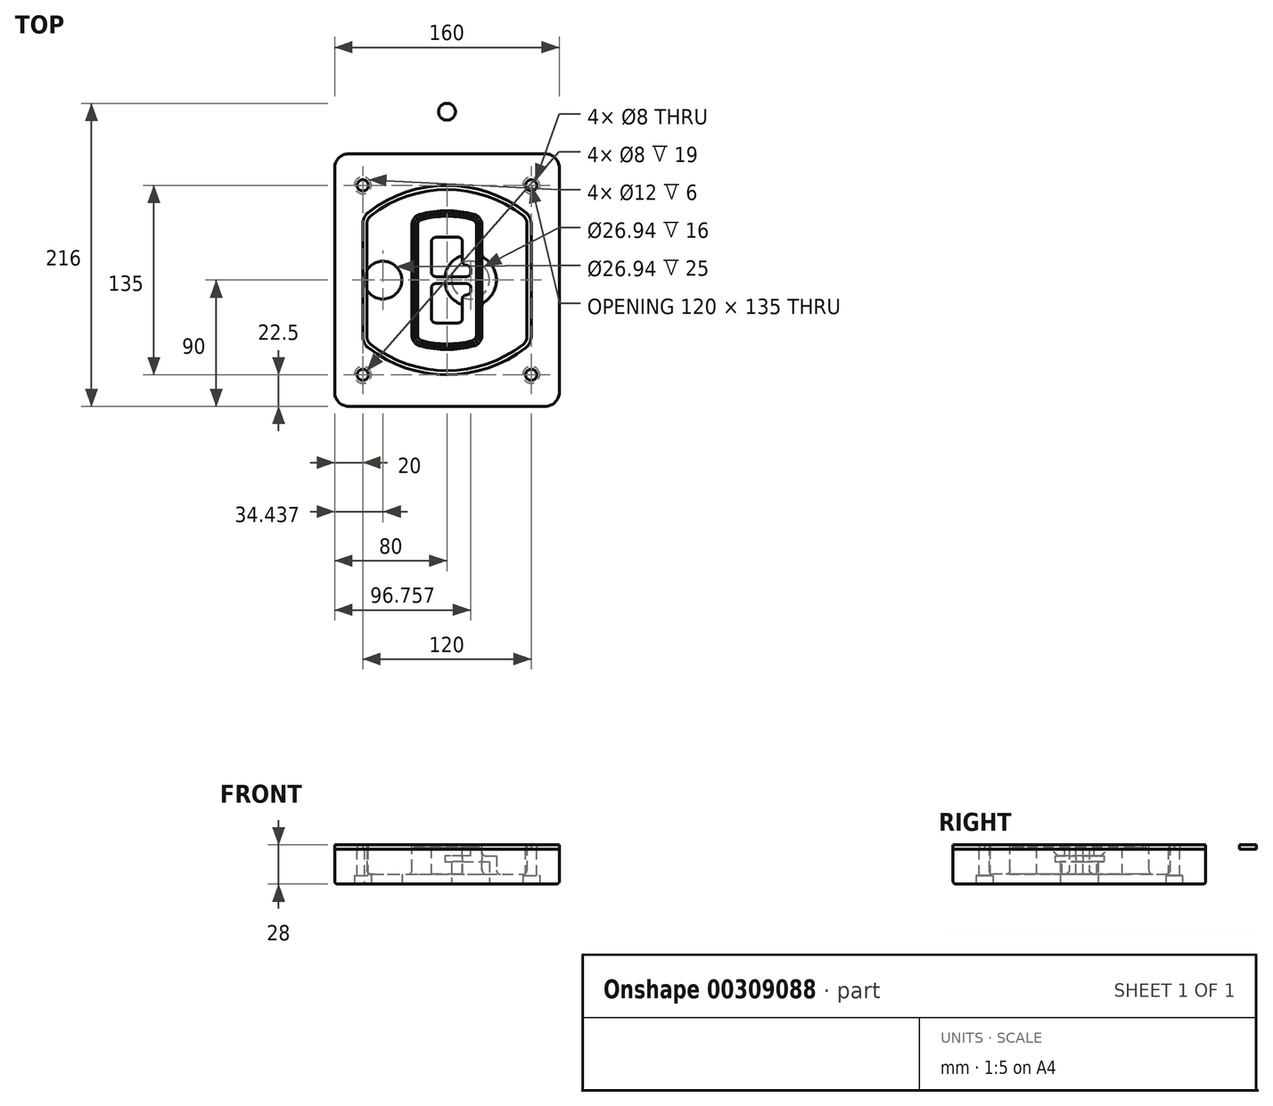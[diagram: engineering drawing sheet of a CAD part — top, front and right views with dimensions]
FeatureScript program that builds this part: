
annotation { "Feature Type Name" : "Feature", "Feature Type Description" : "" }
export const myFeature = defineFeature(function(context is Context, id is Id, definition is map)
    precondition{}
    {
        {
            var Q0;
            Q0=qCreatedBy(makeId("Top.planeOp"),FACE);
            var sketch = newSketch(context, id + "F0", { "sketchPlane" : qUnion([Q0])});
            skPoint(sketch, "E0.rect.middle", {"position": v(0, 0) * mm});
            skLineSegment(sketch, "E1.bottom", {"start": v(-70, -90) * mm, "end": v(70, -90) * mm});
            skLineSegment(sketch, "E1.top", {"start": v(-70, 90) * mm, "end": v(70, 90) * mm});
            skLineSegment(sketch, "E1.left", {"start": v(-80, -80) * mm, "end": v(-80, 80) * mm});
            skLineSegment(sketch, "E1.right", {"start": v(80, -80) * mm, "end": v(80, 80) * mm});
            skLineSegment(sketch, "E2", {"start": v(-80, 90) * mm, "end": v(80, -90) * mm, "construction": true});
            skLineSegment(sketch, "E3", {"start": v(80, 90) * mm, "end": v(-80, -90) * mm, "construction": true});
            skCircle(sketch, "E4", {"center": v(-60, 67.5) * mm, "radius": 4 * mm});
            skCircle(sketch, "E5", {"center": v(60, 67.5) * mm, "radius": 4 * mm});
            skCircle(sketch, "E6", {"center": v(60, -67.5) * mm, "radius": 4 * mm});
            skCircle(sketch, "E7", {"center": v(-60, -67.5) * mm, "radius": 4 * mm});
            skLineSegment(sketch, "E8", {"start": v(-60, 67.5) * mm, "end": v(60, 67.5) * mm, "construction": true});
            skLineSegment(sketch, "E9", {"start": v(60, 67.5) * mm, "end": v(60, -67.5) * mm, "construction": true});
            skLineSegment(sketch, "E10", {"start": v(60, -67.5) * mm, "end": v(-60, -67.5) * mm, "construction": true});
            skLineSegment(sketch, "E11", {"start": v(-60, -67.5) * mm, "end": v(-60, 67.5) * mm, "construction": true});
            skLineSegment(sketch, "E12", {"start": v(-60, 40.3) * mm, "end": v(-60, -40.3) * mm});
            skLineSegment(sketch, "E13", {"start": v(60, 40.3) * mm, "end": v(60, -40.3) * mm});
            skArc(sketch, "E14", {"start": v(56.15, 48.18) * mm, "mid": v(0, 67.5) * mm, "end": v(-56.15, 48.18) * mm});
            skArc(sketch, "E15", {"start": v(-56.15, -48.18) * mm, "mid": v(0, -67.5) * mm, "end": v(56.15, -48.18) * mm});
            skLineSegment(sketch, "E16", {"start": v(-60, 0) * mm, "end": v(60, 0) * mm, "construction": true});
            skPoint(sketch, "E17.visualSharp", {"position": v(-60, -45) * mm});
            skArc(sketch, "E17.filletArc", {"start": v(-60, -40.3) * mm, "mid": v(-58.99, -44.68) * mm, "end": v(-56.15, -48.18) * mm});
            skPoint(sketch, "E18.visualSharp", {"position": v(-60, 45) * mm});
            skArc(sketch, "E18.filletArc", {"start": v(-56.15, 48.18) * mm, "mid": v(-58.99, 44.68) * mm, "end": v(-60, 40.3) * mm});
            skPoint(sketch, "E19.visualSharp", {"position": v(60, 45) * mm});
            skArc(sketch, "E19.filletArc", {"start": v(60, 40.3) * mm, "mid": v(58.99, 44.68) * mm, "end": v(56.15, 48.18) * mm});
            skPoint(sketch, "E20.visualSharp", {"position": v(60, -45) * mm});
            skArc(sketch, "E20.filletArc", {"start": v(56.15, -48.18) * mm, "mid": v(58.99, -44.68) * mm, "end": v(60, -40.3) * mm});
            skPoint(sketch, "E21.visualSharp", {"position": v(-80, 90) * mm});
            skArc(sketch, "E21.filletArc", {"start": v(-70, 90) * mm, "mid": v(-77.07, 87.07) * mm, "end": v(-80, 80) * mm});
            skPoint(sketch, "E22.visualSharp", {"position": v(80, 90) * mm});
            skArc(sketch, "E22.filletArc", {"start": v(80, 80) * mm, "mid": v(77.07, 87.07) * mm, "end": v(70, 90) * mm});
            skPoint(sketch, "E23.visualSharp", {"position": v(80, -90) * mm});
            skArc(sketch, "E23.filletArc", {"start": v(70, -90) * mm, "mid": v(77.07, -87.07) * mm, "end": v(80, -80) * mm});
            skPoint(sketch, "E24.visualSharp", {"position": v(-80, -90) * mm});
            skArc(sketch, "E24.filletArc", {"start": v(-80, -80) * mm, "mid": v(-77.07, -87.07) * mm, "end": v(-70, -90) * mm});
            skArc(sketch, "E25.0", {"start": v(57, 40.3) * mm, "mid": v(56.3, 43.36) * mm, "end": v(54.3, 45.81) * mm});
            skLineSegment(sketch, "E25.1", {"start": v(57, 40.3) * mm, "end": v(57, -40.3) * mm});
            skArc(sketch, "E25.2", {"start": v(54.3, -45.81) * mm, "mid": v(56.3, -43.36) * mm, "end": v(57, -40.3) * mm});
            skArc(sketch, "E25.3", {"start": v(-54.3, -45.81) * mm, "mid": v(0, -64.5) * mm, "end": v(54.3, -45.81) * mm});
            skArc(sketch, "E25.4", {"start": v(-57, -40.3) * mm, "mid": v(-56.3, -43.36) * mm, "end": v(-54.3, -45.81) * mm});
            skArc(sketch, "E25.5", {"start": v(54.3, 45.81) * mm, "mid": v(0, 64.5) * mm, "end": v(-54.3, 45.81) * mm});
            skLineSegment(sketch, "E25.6", {"start": v(-57, 40.3) * mm, "end": v(-57, -40.3) * mm});
            skArc(sketch, "E25.7", {"start": v(-54.3, 45.81) * mm, "mid": v(-56.3, 43.36) * mm, "end": v(-57, 40.3) * mm});
            skArc(sketch, "E26.0", {"start": v(-58.62, 51.33) * mm, "mid": v(-62.58, 46.43) * mm, "end": v(-64, 40.3) * mm});
            skArc(sketch, "E26.1", {"start": v(58.62, 51.33) * mm, "mid": v(0, 71.5) * mm, "end": v(-58.62, 51.33) * mm});
            skArc(sketch, "E26.2", {"start": v(64, 40.3) * mm, "mid": v(62.58, 46.43) * mm, "end": v(58.62, 51.33) * mm});
            skLineSegment(sketch, "E26.3", {"start": v(64, 40.3) * mm, "end": v(64, -40.3) * mm});
            skArc(sketch, "E26.4", {"start": v(58.62, -51.33) * mm, "mid": v(62.58, -46.43) * mm, "end": v(64, -40.3) * mm});
            skLineSegment(sketch, "E26.5", {"start": v(-64, 40.3) * mm, "end": v(-64, -40.3) * mm});
            skArc(sketch, "E26.6", {"start": v(-58.62, -51.33) * mm, "mid": v(0, -71.5) * mm, "end": v(58.62, -51.33) * mm});
            skArc(sketch, "E26.7", {"start": v(-64, -40.3) * mm, "mid": v(-62.58, -46.43) * mm, "end": v(-58.62, -51.33) * mm});
            skSolve(sketch);
        }
        {
            var Q0;
            Q0=makeQuery(id+"F0.imprint","IMPRINT",FACE,{"disambiguationData":[TD([[makeQuery(id+"F0.imprint","IMPRINT",EDGE,{"derivedFrom":sQuery(id+"F0.wireOp",EDGE,"E1.bottom")}),1.0]])]});
            var Q1;
            Q1=makeQuery(id+"F0.imprint","IMPRINT",FACE,{"disambiguationData":[TD([[makeQuery(id+"F0.imprint","IMPRINT",EDGE,{"derivedFrom":sQuery(id+"F0.wireOp",EDGE,"E12")}),1.0]])]});
            var Q2;
            Q2=makeQuery(id+"F0.imprint","IMPRINT",FACE,{"disambiguationData":[TD([[makeQuery(id+"F0.imprint","IMPRINT",EDGE,{"derivedFrom":sQuery(id+"F0.wireOp",EDGE,"E25.0")}),1.0]])]});
            var Q3;
            Q3=makeQuery(id+"F0.imprint","IMPRINT",FACE,{"disambiguationData":[TD([[makeQuery(id+"F0.imprint","IMPRINT",EDGE,{"derivedFrom":sQuery(id+"F0.wireOp",EDGE,"E12")}),-1.0]])]});
            extrude(context, id + "F1", {"entities" : qUnion([Q0, Q1, Q2, Q3]), "oppositeDirection" : true, "depth" : 25 * mm});
        }
        {
            var Q0;
            Q0=makeQuery(id+"F0.imprint","IMPRINT",FACE,{"disambiguationData":[TD([[makeQuery(id+"F0.imprint","IMPRINT",EDGE,{"derivedFrom":sQuery(id+"F0.wireOp",EDGE,"E12")}),1.0]])]});
            extrude(context, id + "F2", {"entities" : qUnion([Q0]), "operationType" : NewBodyOperationType.ADD, "depth" : 3 * mm});
        }
        {
            var Q0;
            Q0=makeQuery(id+"F0.imprint","IMPRINT",FACE,{"disambiguationData":[TD([[makeQuery(id+"F0.imprint","IMPRINT",EDGE,{"derivedFrom":sQuery(id+"F0.wireOp",EDGE,"E25.0")}),1.0]])]});
            extrude(context, id + "F3", {"entities" : qUnion([Q0]), "operationType" : NewBodyOperationType.REMOVE, "oppositeDirection" : true, "depth" : 18 * mm});
        }
        {
            var Q0;
            Q0=makeQuery(id+"F2.opExtrude","CAP_FACE",FACE,{"disambiguationData":[OSD([sQuery(id+"F0.wireOp",EDGE,"E12"),sQuery(id+"F0.wireOp",EDGE,"E13"),sQuery(id+"F0.wireOp",EDGE,"E14"),sQuery(id+"F0.wireOp",EDGE,"E15"),sQuery(id+"F0.wireOp",EDGE,"E17.filletArc"),sQuery(id+"F0.wireOp",EDGE,"E18.filletArc"),sQuery(id+"F0.wireOp",EDGE,"E19.filletArc"),sQuery(id+"F0.wireOp",EDGE,"E20.filletArc"),sQuery(id+"F0.wireOp",EDGE,"E25.0"),sQuery(id+"F0.wireOp",EDGE,"E25.1"),sQuery(id+"F0.wireOp",EDGE,"E25.2"),sQuery(id+"F0.wireOp",EDGE,"E25.3"),sQuery(id+"F0.wireOp",EDGE,"E25.4"),sQuery(id+"F0.wireOp",EDGE,"E25.5"),sQuery(id+"F0.wireOp",EDGE,"E25.6"),sQuery(id+"F0.wireOp",EDGE,"E25.7")])],"isStart":false});
            var sketch = newSketch(context, id + "F4", { "sketchPlane" : qUnion([Q0])});
            skArc(sketch, "E27.0", {"start": v(-19.08, -46.97) * mm, "mid": v(0, -49.5) * mm, "end": v(19.08, -46.97) * mm});
            skArc(sketch, "E28.0", {"start": v(19.08, 46.97) * mm, "mid": v(0, 49.5) * mm, "end": v(-19.08, 46.97) * mm});
            skLineSegment(sketch, "E29", {"start": v(-25, 39.25) * mm, "end": v(-25, -39.25) * mm});
            skLineSegment(sketch, "E30", {"start": v(25, 39.25) * mm, "end": v(25, -39.25) * mm});
            skLineSegment(sketch, "E31", {"start": v(-25, 45.1) * mm, "end": v(25, 45.1) * mm, "construction": true});
            skLineSegment(sketch, "E32", {"start": v(-25, -45.1) * mm, "end": v(25, -45.1) * mm, "construction": true});
            skPoint(sketch, "E33.visualSharp", {"position": v(-25, 45.1) * mm});
            skArc(sketch, "E33.filletArc", {"start": v(-19.08, 46.97) * mm, "mid": v(-23.35, 44.11) * mm, "end": v(-25, 39.25) * mm});
            skPoint(sketch, "E34.visualSharp", {"position": v(25, 45.1) * mm});
            skArc(sketch, "E34.filletArc", {"start": v(25, 39.25) * mm, "mid": v(23.35, 44.11) * mm, "end": v(19.08, 46.97) * mm});
            skPoint(sketch, "E35.visualSharp", {"position": v(25, -45.1) * mm});
            skArc(sketch, "E35.filletArc", {"start": v(19.08, -46.97) * mm, "mid": v(23.35, -44.11) * mm, "end": v(25, -39.25) * mm});
            skPoint(sketch, "E36.visualSharp", {"position": v(-25, -45.1) * mm});
            skArc(sketch, "E36.filletArc", {"start": v(-25, -39.25) * mm, "mid": v(-23.35, -44.11) * mm, "end": v(-19.08, -46.97) * mm});
            skArc(sketch, "E37.0", {"start": v(54.3, 45.81) * mm, "mid": v(0, 64.5) * mm, "end": v(-54.3, 45.81) * mm});
            skArc(sketch, "E37.1", {"start": v(-54.3, 45.81) * mm, "mid": v(-56.3, 43.36) * mm, "end": v(-57, 40.3) * mm});
            skLineSegment(sketch, "E37.2", {"start": v(-57, 40.3) * mm, "end": v(-57, -40.3) * mm});
            skArc(sketch, "E37.3", {"start": v(-57, -40.3) * mm, "mid": v(-56.3, -43.36) * mm, "end": v(-54.3, -45.81) * mm});
            skArc(sketch, "E37.4", {"start": v(-54.3, -45.81) * mm, "mid": v(0, -64.5) * mm, "end": v(54.3, -45.81) * mm});
            skArc(sketch, "E37.5", {"start": v(54.3, -45.81) * mm, "mid": v(56.3, -43.36) * mm, "end": v(57, -40.3) * mm});
            skLineSegment(sketch, "E37.6", {"start": v(57, 40.3) * mm, "end": v(57, -40.3) * mm});
            skArc(sketch, "E37.7", {"start": v(57, 40.3) * mm, "mid": v(56.3, 43.36) * mm, "end": v(54.3, 45.81) * mm});
            skLineSegment(sketch, "E38.0", {"start": v(23, 39.25) * mm, "end": v(23, -39.25) * mm});
            skArc(sketch, "E38.1", {"start": v(18.56, -45.04) * mm, "mid": v(21.76, -42.9) * mm, "end": v(23, -39.25) * mm});
            skArc(sketch, "E38.2", {"start": v(-18.56, -45.04) * mm, "mid": v(0, -47.5) * mm, "end": v(18.56, -45.04) * mm});
            skArc(sketch, "E38.3", {"start": v(-23, -39.25) * mm, "mid": v(-21.76, -42.9) * mm, "end": v(-18.56, -45.04) * mm});
            skLineSegment(sketch, "E38.4", {"start": v(-23, 39.25) * mm, "end": v(-23, -39.25) * mm});
            skArc(sketch, "E38.5", {"start": v(23, 39.25) * mm, "mid": v(21.76, 42.9) * mm, "end": v(18.56, 45.04) * mm});
            skArc(sketch, "E38.6", {"start": v(-18.56, 45.04) * mm, "mid": v(-21.76, 42.9) * mm, "end": v(-23, 39.25) * mm});
            skArc(sketch, "E38.7", {"start": v(18.56, 45.04) * mm, "mid": v(0, 47.5) * mm, "end": v(-18.56, 45.04) * mm});
            skArc(sketch, "E39.0", {"start": v(21, 39.25) * mm, "mid": v(20.18, 41.68) * mm, "end": v(18.04, 43.1) * mm});
            skLineSegment(sketch, "E39.1", {"start": v(21, 39.25) * mm, "end": v(21, -39.25) * mm});
            skArc(sketch, "E39.2", {"start": v(18.04, -43.1) * mm, "mid": v(20.18, -41.68) * mm, "end": v(21, -39.25) * mm});
            skArc(sketch, "E39.3", {"start": v(-18.04, -43.1) * mm, "mid": v(0, -45.5) * mm, "end": v(18.04, -43.1) * mm});
            skArc(sketch, "E39.4", {"start": v(-21, -39.25) * mm, "mid": v(-20.18, -41.68) * mm, "end": v(-18.04, -43.1) * mm});
            skArc(sketch, "E39.5", {"start": v(18.04, 43.1) * mm, "mid": v(0, 45.5) * mm, "end": v(-18.04, 43.1) * mm});
            skLineSegment(sketch, "E39.6", {"start": v(-21, 39.25) * mm, "end": v(-21, -39.25) * mm});
            skArc(sketch, "E39.7", {"start": v(-18.04, 43.1) * mm, "mid": v(-20.18, 41.68) * mm, "end": v(-21, 39.25) * mm});
            skLineSegment(sketch, "E40", {"start": v(-25, 0) * mm, "end": v(25, 0) * mm, "construction": true});
            skLineSegment(sketch, "E41", {"start": v(-11, 5.5) * mm, "end": v(-11, 27.5) * mm});
            skLineSegment(sketch, "E42", {"start": v(-8, 30.5) * mm, "end": v(8, 30.5) * mm});
            skLineSegment(sketch, "E43", {"start": v(11, 27.5) * mm, "end": v(11, 13.5) * mm});
            skLineSegment(sketch, "E44", {"start": v(14, 10.5) * mm, "end": v(14, 10.5) * mm});
            skLineSegment(sketch, "E45", {"start": v(17, 7.5) * mm, "end": v(17, 5.5) * mm});
            skLineSegment(sketch, "E46", {"start": v(14, 2.5) * mm, "end": v(-8, 2.5) * mm});
            skPoint(sketch, "E47.visualSharp", {"position": v(-11, 30.5) * mm});
            skArc(sketch, "E47.filletArc", {"start": v(-8, 30.5) * mm, "mid": v(-10.12, 29.62) * mm, "end": v(-11, 27.5) * mm});
            skPoint(sketch, "E48.visualSharp", {"position": v(11, 30.5) * mm});
            skArc(sketch, "E48.filletArc", {"start": v(11, 27.5) * mm, "mid": v(10.12, 29.62) * mm, "end": v(8, 30.5) * mm});
            skPoint(sketch, "E49.visualSharp", {"position": v(11, 10.5) * mm});
            skArc(sketch, "E49.filletArc", {"start": v(11, 13.5) * mm, "mid": v(11.88, 11.38) * mm, "end": v(14, 10.5) * mm});
            skPoint(sketch, "E50.visualSharp", {"position": v(17, 10.5) * mm});
            skArc(sketch, "E50.filletArc", {"start": v(17, 7.5) * mm, "mid": v(16.12, 9.62) * mm, "end": v(14, 10.5) * mm});
            skPoint(sketch, "E51.visualSharp", {"position": v(17, 2.5) * mm});
            skArc(sketch, "E51.filletArc", {"start": v(14, 2.5) * mm, "mid": v(16.12, 3.38) * mm, "end": v(17, 5.5) * mm});
            skPoint(sketch, "E52.visualSharp", {"position": v(-11, 2.5) * mm});
            skArc(sketch, "E52.filletArc", {"start": v(-11, 5.5) * mm, "mid": v(-10.12, 3.38) * mm, "end": v(-8, 2.5) * mm});
            skLineSegment(sketch, "E53.0.MirrorCS", {"start": v(14, -2.5) * mm, "end": v(-8, -2.5) * mm});
            skArc(sketch, "E54.0.MirrorCS", {"start": v(-11, -5.5) * mm, "mid": v(-10.12, -3.38) * mm, "end": v(-8, -2.5) * mm});
            skLineSegment(sketch, "E55.0.MirrorCS", {"start": v(-11, -5.5) * mm, "end": v(-11, -27.5) * mm});
            skArc(sketch, "E56.0.MirrorCS", {"start": v(-8, -30.5) * mm, "mid": v(-10.12, -29.62) * mm, "end": v(-11, -27.5) * mm});
            skLineSegment(sketch, "E57.0.MirrorCS", {"start": v(-8, -30.5) * mm, "end": v(8, -30.5) * mm});
            skArc(sketch, "E58.0.MirrorCS", {"start": v(11, -27.5) * mm, "mid": v(10.12, -29.62) * mm, "end": v(8, -30.5) * mm});
            skLineSegment(sketch, "E59.0.MirrorCS", {"start": v(11, -27.5) * mm, "end": v(11, -13.5) * mm});
            skArc(sketch, "E60.0.MirrorCS", {"start": v(11, -13.5) * mm, "mid": v(11.88, -11.38) * mm, "end": v(14, -10.5) * mm});
            skArc(sketch, "E61.0.MirrorCS", {"start": v(17, -7.5) * mm, "mid": v(16.12, -9.62) * mm, "end": v(14, -10.5) * mm});
            skLineSegment(sketch, "E62.0.MirrorCS", {"start": v(17, -7.5) * mm, "end": v(17, -5.5) * mm});
            skArc(sketch, "E63.0.MirrorCS", {"start": v(14, -2.5) * mm, "mid": v(16.12, -3.38) * mm, "end": v(17, -5.5) * mm});
            skSolve(sketch);
        }
        {
            var Q0;
            Q0=makeQuery(id+"F4.imprint","IMPRINT",FACE,{"disambiguationData":[TD([[makeQuery(id+"F4.imprint","IMPRINT",EDGE,{"derivedFrom":sQuery(id+"F4.wireOp",EDGE,"E27.0")}),1.0]])]});
            var Q1;
            Q1=makeQuery(id+"F4.imprint","IMPRINT",FACE,{"disambiguationData":[TD([[makeQuery(id+"F4.imprint","IMPRINT",EDGE,{"derivedFrom":sQuery(id+"F4.wireOp",EDGE,"E38.0")}),-1.0]])]});
            var Q2;
            Q2=makeQuery(id+"F4.imprint","IMPRINT",FACE,{"disambiguationData":[TD([[makeQuery(id+"F4.imprint","IMPRINT",EDGE,{"derivedFrom":sQuery(id+"F4.wireOp",EDGE,"E39.0")}),1.0]])]});
            extrude(context, id + "F5", {"entities" : qUnion([Q0, Q1, Q2]), "operationType" : NewBodyOperationType.ADD, "endBound" : BoundingType.UP_TO_NEXT, "oppositeDirection" : true, "depth" : 25 * mm});
        }
        {
            var Q0;
            Q0=makeQuery(id+"F4.imprint","IMPRINT",FACE,{"disambiguationData":[TD([[makeQuery(id+"F4.imprint","IMPRINT",EDGE,{"derivedFrom":sQuery(id+"F4.wireOp",EDGE,"E38.0")}),-1.0]])]});
            extrude(context, id + "F6", {"entities" : qUnion([Q0]), "operationType" : NewBodyOperationType.REMOVE, "oppositeDirection" : true, "depth" : 2 * mm});
        }
        {
            var Q0;
            Q0=makeQuery(id+"F1.opExtrude","CAP_FACE",FACE,{"disambiguationData":[OSD([sQuery(id+"F0.wireOp",EDGE,"E1.bottom"),sQuery(id+"F0.wireOp",EDGE,"E1.top"),sQuery(id+"F0.wireOp",EDGE,"E1.left"),sQuery(id+"F0.wireOp",EDGE,"E1.right"),sQuery(id+"F0.wireOp",EDGE,"E4"),sQuery(id+"F0.wireOp",EDGE,"E5"),sQuery(id+"F0.wireOp",EDGE,"E6"),sQuery(id+"F0.wireOp",EDGE,"E7"),sQuery(id+"F0.wireOp",EDGE,"E21.filletArc"),sQuery(id+"F0.wireOp",EDGE,"E22.filletArc"),sQuery(id+"F0.wireOp",EDGE,"E23.filletArc"),sQuery(id+"F0.wireOp",EDGE,"E24.filletArc")])],"isStart":false});
            var sketch = newSketch(context, id + "F7", { "sketchPlane" : qUnion([Q0])});
            skCircle(sketch, "E64", {"center": v(16.76, 0) * mm, "radius": 13.47 * mm});
            skCircle(sketch, "E65", {"center": v(-45.56, 0) * mm, "radius": 13.47 * mm});
            skLineSegment(sketch, "E66", {"start": v(80, 0) * mm, "end": v(-80, 0) * mm});
            skCircle(sketch, "E67", {"center": v(16.76, 0) * mm, "radius": 18.47 * mm});
            skCircle(sketch, "E68", {"center": v(60, -67.5) * mm, "radius": 6 * mm});
            skCircle(sketch, "E69", {"center": v(-60, -67.5) * mm, "radius": 6 * mm});
            skCircle(sketch, "E70", {"center": v(-60, 67.5) * mm, "radius": 6 * mm});
            skCircle(sketch, "E71", {"center": v(60, 67.5) * mm, "radius": 6 * mm});
            skSolve(sketch);
        }
        {
            var Q0;
            {var subQ1=sQuery(id+"F7.wireOp",EDGE,"E66");var subQ4=sQuery(id+"F7.wireOp",EDGE,"E64");var subQ6=makeQuery(id+"F7.imprint","INTERSECT",VERTEX,{"disambiguationData":[OD(0.0)],"derivedFrom":[subQ4,subQ1]});Q0=makeQuery(id+"F7.imprint","IMPRINT",FACE,{"disambiguationData":[TD([[makeQuery(id+"F7.imprint","IMPRINT",EDGE,{"disambiguationData":[TD([[subQ6,-1.0]])],"derivedFrom":subQ4}),-1.0]])]});}
            var Q1;
            {var subQ0=sQuery(id+"F7.wireOp",EDGE,"E66");var subQ1=sQuery(id+"F7.wireOp",EDGE,"E64");var subQ3=makeQuery(id+"F7.imprint","INTERSECT",VERTEX,{"disambiguationData":[OD(0.0)],"derivedFrom":[subQ1,subQ0]});Q1=makeQuery(id+"F7.imprint","IMPRINT",FACE,{"disambiguationData":[TD([[makeQuery(id+"F7.imprint","IMPRINT",EDGE,{"disambiguationData":[TD([[subQ3,-1.0]])],"derivedFrom":subQ1}),1.0]])]});}
            var Q2;
            {var subQ0=sQuery(id+"F7.wireOp",EDGE,"E66");var subQ1=sQuery(id+"F7.wireOp",EDGE,"E64");var subQ3=makeQuery(id+"F7.imprint","INTERSECT",VERTEX,{"disambiguationData":[OD(0.0)],"derivedFrom":[subQ1,subQ0]});Q2=makeQuery(id+"F7.imprint","IMPRINT",FACE,{"disambiguationData":[TD([[makeQuery(id+"F7.imprint","IMPRINT",EDGE,{"disambiguationData":[TD([[subQ3,1.0]])],"derivedFrom":subQ1}),1.0]])]});}
            var Q3;
            {var subQ1=sQuery(id+"F7.wireOp",EDGE,"E66");var subQ4=sQuery(id+"F7.wireOp",EDGE,"E64");var subQ6=makeQuery(id+"F7.imprint","INTERSECT",VERTEX,{"disambiguationData":[OD(0.0)],"derivedFrom":[subQ4,subQ1]});Q3=makeQuery(id+"F7.imprint","IMPRINT",FACE,{"disambiguationData":[TD([[makeQuery(id+"F7.imprint","IMPRINT",EDGE,{"disambiguationData":[TD([[subQ6,1.0]])],"derivedFrom":subQ4}),-1.0]])]});}
            extrude(context, id + "F8", {"entities" : qUnion([Q0, Q1, Q2, Q3]), "operationType" : NewBodyOperationType.ADD, "oppositeDirection" : true, "depth" : 20 * mm});
        }
        {
            var Q0;
            {var subQ0=sQuery(id+"F7.wireOp",EDGE,"E66");var subQ1=sQuery(id+"F7.wireOp",EDGE,"E64");var subQ3=makeQuery(id+"F7.imprint","INTERSECT",VERTEX,{"disambiguationData":[OD(0.0)],"derivedFrom":[subQ1,subQ0]});Q0=makeQuery(id+"F7.imprint","IMPRINT",FACE,{"disambiguationData":[TD([[makeQuery(id+"F7.imprint","IMPRINT",EDGE,{"disambiguationData":[TD([[subQ3,-1.0]])],"derivedFrom":subQ1}),1.0]])]});}
            var Q1;
            {var subQ0=sQuery(id+"F7.wireOp",EDGE,"E66");var subQ1=sQuery(id+"F7.wireOp",EDGE,"E64");var subQ3=makeQuery(id+"F7.imprint","INTERSECT",VERTEX,{"disambiguationData":[OD(0.0)],"derivedFrom":[subQ1,subQ0]});Q1=makeQuery(id+"F7.imprint","IMPRINT",FACE,{"disambiguationData":[TD([[makeQuery(id+"F7.imprint","IMPRINT",EDGE,{"disambiguationData":[TD([[subQ3,1.0]])],"derivedFrom":subQ1}),1.0]])]});}
            extrude(context, id + "F9", {"entities" : qUnion([Q0, Q1]), "operationType" : NewBodyOperationType.REMOVE, "oppositeDirection" : true, "depth" : 16 * mm});
        }
        {
            var Q0;
            {var subQ0=sQuery(id+"F7.wireOp",EDGE,"E66");var subQ1=sQuery(id+"F7.wireOp",EDGE,"E65");var subQ3=makeQuery(id+"F7.imprint","INTERSECT",VERTEX,{"disambiguationData":[OD(0.0)],"derivedFrom":[subQ1,subQ0]});Q0=makeQuery(id+"F7.imprint","IMPRINT",FACE,{"disambiguationData":[TD([[makeQuery(id+"F7.imprint","IMPRINT",EDGE,{"disambiguationData":[TD([[subQ3,-1.0]])],"derivedFrom":subQ1}),1.0]])]});}
            var Q1;
            {var subQ0=sQuery(id+"F7.wireOp",EDGE,"E66");var subQ1=sQuery(id+"F7.wireOp",EDGE,"E65");var subQ3=makeQuery(id+"F7.imprint","INTERSECT",VERTEX,{"disambiguationData":[OD(0.0)],"derivedFrom":[subQ1,subQ0]});Q1=makeQuery(id+"F7.imprint","IMPRINT",FACE,{"disambiguationData":[TD([[makeQuery(id+"F7.imprint","IMPRINT",EDGE,{"disambiguationData":[TD([[subQ3,1.0]])],"derivedFrom":subQ1}),1.0]])]});}
            extrude(context, id + "F10", {"entities" : qUnion([Q0, Q1]), "operationType" : NewBodyOperationType.REMOVE, "oppositeDirection" : true, "depth" : 25 * mm});
        }
        {
            var Q0;
            Q0=makeQuery(id+"F7.imprint","IMPRINT",FACE,{"disambiguationData":[TD([[makeQuery(id+"F7.imprint","IMPRINT",EDGE,{"derivedFrom":sQuery(id+"F7.wireOp",EDGE,"E68")}),1.0]])]});
            var Q1;
            Q1=makeQuery(id+"F7.imprint","IMPRINT",FACE,{"disambiguationData":[TD([[makeQuery(id+"F7.imprint","IMPRINT",EDGE,{"derivedFrom":makeQuery(id+"F1.opExtrude","CAP_EDGE",EDGE,{"disambiguationData":[OSD([sQuery(id+"F0.wireOp",EDGE,"E5")])],"isStart":false})}),-1.0]])]});
            var Q2;
            Q2=makeQuery(id+"F7.imprint","IMPRINT",FACE,{"disambiguationData":[TD([[makeQuery(id+"F7.imprint","IMPRINT",EDGE,{"derivedFrom":sQuery(id+"F7.wireOp",EDGE,"E69")}),1.0]])]});
            var Q3;
            Q3=makeQuery(id+"F7.imprint","IMPRINT",FACE,{"disambiguationData":[TD([[makeQuery(id+"F7.imprint","IMPRINT",EDGE,{"derivedFrom":makeQuery(id+"F1.opExtrude","CAP_EDGE",EDGE,{"disambiguationData":[OSD([sQuery(id+"F0.wireOp",EDGE,"E4")])],"isStart":false})}),-1.0]])]});
            var Q4;
            Q4=makeQuery(id+"F7.imprint","IMPRINT",FACE,{"disambiguationData":[TD([[makeQuery(id+"F7.imprint","IMPRINT",EDGE,{"derivedFrom":sQuery(id+"F7.wireOp",EDGE,"E70")}),1.0]])]});
            var Q5;
            Q5=makeQuery(id+"F7.imprint","IMPRINT",FACE,{"disambiguationData":[TD([[makeQuery(id+"F7.imprint","IMPRINT",EDGE,{"derivedFrom":makeQuery(id+"F1.opExtrude","CAP_EDGE",EDGE,{"disambiguationData":[OSD([sQuery(id+"F0.wireOp",EDGE,"E7")])],"isStart":false})}),-1.0]])]});
            var Q6;
            Q6=makeQuery(id+"F7.imprint","IMPRINT",FACE,{"disambiguationData":[TD([[makeQuery(id+"F7.imprint","IMPRINT",EDGE,{"derivedFrom":sQuery(id+"F7.wireOp",EDGE,"E71")}),1.0]])]});
            var Q7;
            Q7=makeQuery(id+"F7.imprint","IMPRINT",FACE,{"disambiguationData":[TD([[makeQuery(id+"F7.imprint","IMPRINT",EDGE,{"derivedFrom":makeQuery(id+"F1.opExtrude","CAP_EDGE",EDGE,{"disambiguationData":[OSD([sQuery(id+"F0.wireOp",EDGE,"E6")])],"isStart":false})}),-1.0]])]});
            extrude(context, id + "F11", {"entities" : qUnion([Q0, Q1, Q2, Q3, Q4, Q5, Q6, Q7]), "operationType" : NewBodyOperationType.REMOVE, "oppositeDirection" : true, "depth" : 6 * mm});
        }
        {
            var Q0;
            Q0=makeQuery(id+"F9.boolean.opBoolean","COPY",FACE,{"derivedFrom":makeQuery(id+"F9.opExtrude","CAP_FACE",FACE,{"disambiguationData":[OSD([sQuery(id+"F7.wireOp",EDGE,"E64")])],"isStart":false})});
            var sketch = newSketch(context, id + "F12", { "sketchPlane" : qUnion([Q0])});
            skArc(sketch, "E72.0", {"start": v(11, 17.55) * mm, "mid": v(2.57, 11.82) * mm, "end": v(-1.54, 2.5) * mm});
            skArc(sketch, "E72.1", {"start": v(-1.54, -2.5) * mm, "mid": v(2.57, -11.82) * mm, "end": v(11, -17.55) * mm});
            skLineSegment(sketch, "E73", {"start": v(-1.54, -2.5) * mm, "end": v(14, -2.5) * mm});
            skLineSegment(sketch, "E74.0", {"start": v(14, 2.5) * mm, "end": v(-1.54, 2.5) * mm});
            skArc(sketch, "E74.1", {"start": v(14, 2.5) * mm, "mid": v(16.12, 3.38) * mm, "end": v(17, 5.5) * mm});
            skLineSegment(sketch, "E74.2", {"start": v(17, 7.5) * mm, "end": v(17, 5.5) * mm});
            skArc(sketch, "E74.3", {"start": v(17, 7.5) * mm, "mid": v(16.12, 9.62) * mm, "end": v(14, 10.5) * mm});
            skArc(sketch, "E74.4", {"start": v(11, 13.5) * mm, "mid": v(11.88, 11.38) * mm, "end": v(14, 10.5) * mm});
            skLineSegment(sketch, "E74.5", {"start": v(11, 17.55) * mm, "end": v(11, 13.5) * mm});
            skLineSegment(sketch, "E74.7", {"start": v(14, -2.5) * mm, "end": v(-1.54, -2.5) * mm});
            skArc(sketch, "E74.8", {"start": v(14, -2.5) * mm, "mid": v(16.12, -3.38) * mm, "end": v(17, -5.5) * mm});
            skLineSegment(sketch, "E74.9", {"start": v(17, -7.5) * mm, "end": v(17, -5.5) * mm});
            skArc(sketch, "E74.10", {"start": v(17, -7.5) * mm, "mid": v(16.12, -9.62) * mm, "end": v(14, -10.5) * mm});
            skArc(sketch, "E74.11", {"start": v(11, -13.5) * mm, "mid": v(11.88, -11.38) * mm, "end": v(14, -10.5) * mm});
            skLineSegment(sketch, "E74.12", {"start": v(11, -17.55) * mm, "end": v(11, -13.5) * mm});
            skPoint(sketch, "E75.orphan", {"position": v(11, -27.5) * mm});
            skPoint(sketch, "E76.orphan", {"position": v(-8, -2.5) * mm});
            skPoint(sketch, "E77.orphan", {"position": v(-8, 2.5) * mm});
            skPoint(sketch, "E78.orphan", {"position": v(11, 27.5) * mm});
            skSolve(sketch);
        }
        {
            var Q0;
            {var subQ7=sQuery(id+"F12.wireOp",EDGE,"E72.0");var subQ14=sQuery(id+"F12.wireOp",EDGE,"E72.1");var subQ16=sQuery(id+"F12.wireOp",EDGE,"E74.1");var subQ18=sQuery(id+"F12.wireOp",EDGE,"E74.8");Q0=qUnion([makeQuery(id+"F12.imprint","IMPRINT",FACE,{"disambiguationData":[TD([[makeQuery(id+"F12.imprint","IMPRINT",EDGE,{"derivedFrom":subQ7}),1.0]])]}),makeQuery(id+"F12.imprint","IMPRINT",FACE,{"disambiguationData":[TD([[makeQuery(id+"F12.imprint","IMPRINT",EDGE,{"derivedFrom":subQ14}),1.0]])]}),makeQuery(id+"F12.imprint","IMPRINT",FACE,{"disambiguationData":[TD([[makeQuery(id+"F12.imprint","IMPRINT",EDGE,{"derivedFrom":subQ16}),1.0]])]}),makeQuery(id+"F12.imprint","IMPRINT",FACE,{"disambiguationData":[TD([[makeQuery(id+"F12.imprint","IMPRINT",EDGE,{"derivedFrom":subQ18}),-1.0]])]})]);}
            var Q1;
            Q1=makeQuery(id+"F5.boolean.opBoolean","SPLIT",FACE,{"disambiguationData":[TD([makeQuery(id+"F5.opExtrude","SWEPT_FACE",FACE,{"disambiguationData":[OSD([sQuery(id+"F4.wireOp",EDGE,"E41")])]})])],"derivedFrom":makeQuery(id+"F3.boolean.opBoolean","COPY",FACE,{"derivedFrom":makeQuery(id+"F3.opExtrude","CAP_FACE",FACE,{"disambiguationData":[OSD([sQuery(id+"F0.wireOp",EDGE,"E25.0"),sQuery(id+"F0.wireOp",EDGE,"E25.1"),sQuery(id+"F0.wireOp",EDGE,"E25.2"),sQuery(id+"F0.wireOp",EDGE,"E25.3"),sQuery(id+"F0.wireOp",EDGE,"E25.4"),sQuery(id+"F0.wireOp",EDGE,"E25.5"),sQuery(id+"F0.wireOp",EDGE,"E25.6"),sQuery(id+"F0.wireOp",EDGE,"E25.7")])],"isStart":false})})});
            extrude(context, id + "F13", {"entities" : qUnion([Q0]), "operationType" : NewBodyOperationType.REMOVE, "endBound" : BoundingType.UP_TO_SURFACE, "endBoundEntityFace" : qUnion([Q1]), "depth" : 25 * mm});
        }
        {
            var Q0;
            Q0=makeQuery(id+"F3.boolean.opBoolean","COPY",EDGE,{"derivedFrom":makeQuery(id+"F3.opExtrude","CAP_EDGE",EDGE,{"disambiguationData":[OSD([sQuery(id+"F0.wireOp",EDGE,"E25.6")])],"isStart":false})});
            var Q1;
            Q1=makeQuery(id+"F8.boolean.opBoolean","INTERSECT",EDGE,{"derivedFrom":[makeQuery(id+"F5.opExtrude","SWEPT_FACE",FACE,{"disambiguationData":[OSD([sQuery(id+"F4.wireOp",EDGE,"E30")])]}),makeQuery(id+"F8.opExtrude","CAP_FACE",FACE,{"disambiguationData":[OSD([sQuery(id+"F7.wireOp",EDGE,"E67")])],"isStart":false})]});
            var Q2;
            Q2=makeQuery(id+"F8.boolean.opBoolean","INTERSECT",EDGE,{"disambiguationData":[OD(1.0)],"derivedFrom":[makeQuery(id+"F5.opExtrude","SWEPT_FACE",FACE,{"disambiguationData":[OSD([sQuery(id+"F4.wireOp",EDGE,"E30")])]}),makeQuery(id+"F8.opExtrude","SWEPT_FACE",FACE,{"disambiguationData":[OSD([sQuery(id+"F7.wireOp",EDGE,"E67")])]})]});
            var Q3;
            {var subQ0=sQuery(id+"F4.wireOp",EDGE,"E30");Q3=makeQuery(id+"F8.boolean.opBoolean","SPLIT",EDGE,{"disambiguationData":[TD([makeQuery(id+"F5.opExtrude","SWEPT_FACE",FACE,{"disambiguationData":[OSD([sQuery(id+"F4.wireOp",EDGE,"E35.filletArc")])]})])],"derivedFrom":makeQuery(id+"F5.opExtrude","CAP_EDGE",EDGE,{"disambiguationData":[OSD([subQ0])],"isStart":false})});}
            var Q4;
            {var subQ0=sQuery(id+"F0.wireOp",EDGE,"E25.7");var subQ1=sQuery(id+"F0.wireOp",EDGE,"E25.1");var subQ2=sQuery(id+"F0.wireOp",EDGE,"E25.6");var subQ3=sQuery(id+"F0.wireOp",EDGE,"E25.5");var subQ4=sQuery(id+"F0.wireOp",EDGE,"E25.4");var subQ5=sQuery(id+"F0.wireOp",EDGE,"E25.0");var subQ6=sQuery(id+"F0.wireOp",EDGE,"E25.2");var subQ7=sQuery(id+"F0.wireOp",EDGE,"E25.3");Q4=makeQuery(id+"F8.boolean.opBoolean","INTERSECT",EDGE,{"derivedFrom":[makeQuery(id+"F5.boolean.opBoolean","SPLIT",FACE,{"disambiguationData":[TD([makeQuery(id+"F2.opExtrude","SWEPT_FACE",FACE,{"disambiguationData":[OSD([subQ5])]})])],"derivedFrom":makeQuery(id+"F3.boolean.opBoolean","COPY",FACE,{"derivedFrom":makeQuery(id+"F3.opExtrude","CAP_FACE",FACE,{"disambiguationData":[OSD([subQ5,subQ1,subQ6,subQ7,subQ4,subQ3,subQ2,subQ0])],"isStart":false})})}),makeQuery(id+"F8.opExtrude","SWEPT_FACE",FACE,{"disambiguationData":[OSD([sQuery(id+"F7.wireOp",EDGE,"E67")])]})]});}
            var Q5;
            Q5=makeQuery(id+"F8.boolean.opBoolean","INTERSECT",EDGE,{"disambiguationData":[OD(0.0)],"derivedFrom":[makeQuery(id+"F5.opExtrude","SWEPT_FACE",FACE,{"disambiguationData":[OSD([sQuery(id+"F4.wireOp",EDGE,"E30")])]}),makeQuery(id+"F8.opExtrude","SWEPT_FACE",FACE,{"disambiguationData":[OSD([sQuery(id+"F7.wireOp",EDGE,"E67")])]})]});
            fillet(context, id + "F14", {"entities" : qUnion([Q0, Q1, Q2, Q3, Q4, Q5]), "radius" : 3 * mm, "tangentPropagation" : true, "allowEdgeOverflow" : false});
        }
        {
            var Q0;
            Q0=makeQuery(id+"F1.opExtrude","CAP_EDGE",EDGE,{"disambiguationData":[OSD([sQuery(id+"F0.wireOp",EDGE,"E1.bottom")])],"isStart":false});
            fillet(context, id + "F15", {"entities" : qUnion([Q0]), "radius" : 2 * mm, "tangentPropagation" : true, "allowEdgeOverflow" : false});
        }
        {
            var Q0;
            {var subQ0=sQuery(id+"F0.wireOp",EDGE,"E21.filletArc");var subQ1=sQuery(id+"F0.wireOp",EDGE,"E7");var subQ2=sQuery(id+"F0.wireOp",EDGE,"E6");var subQ3=sQuery(id+"F0.wireOp",EDGE,"E5");var subQ4=sQuery(id+"F0.wireOp",EDGE,"E4");var subQ5=sQuery(id+"F0.wireOp",EDGE,"E22.filletArc");var subQ6=sQuery(id+"F0.wireOp",EDGE,"E1.bottom");var subQ7=sQuery(id+"F0.wireOp",EDGE,"E1.right");var subQ8=sQuery(id+"F0.wireOp",EDGE,"E1.top");var subQ9=sQuery(id+"F0.wireOp",EDGE,"E1.left");var subQ10=sQuery(id+"F0.wireOp",EDGE,"E23.filletArc");var subQ11=sQuery(id+"F0.wireOp",EDGE,"E24.filletArc");Q0=makeQuery(id+"F2.boolean.opBoolean","SPLIT",FACE,{"disambiguationData":[TD([makeQuery(id+"F1.opExtrude","SWEPT_FACE",FACE,{"disambiguationData":[OSD([subQ6])]})])],"derivedFrom":makeQuery(id+"F1.opExtrude","CAP_FACE",FACE,{"disambiguationData":[OSD([subQ6,subQ8,subQ9,subQ7,subQ4,subQ3,subQ2,subQ1,subQ0,subQ5,subQ10,subQ11])],"isStart":true})});}
            var sketch = newSketch(context, id + "F16", { "sketchPlane" : qUnion([Q0])});
            skLineSegment(sketch, "E79", {"start": v(-33, 90) * mm, "end": v(-15, 108) * mm});
            skLineSegment(sketch, "E80", {"start": v(-15, 108) * mm, "end": v(-15, 120) * mm});
            skLineSegment(sketch, "E81", {"start": v(15, 120) * mm, "end": v(15, 108) * mm});
            skLineSegment(sketch, "E82", {"start": v(15, 108) * mm, "end": v(33, 90) * mm});
            skArc(sketch, "E83", {"start": v(15, 120) * mm, "mid": v(0, 135) * mm, "end": v(-15, 120) * mm});
            skCircle(sketch, "E84", {"center": v(0, 120) * mm, "radius": 6 * mm});
            skLineSegment(sketch, "E85", {"start": v(0, 120) * mm, "end": v(0, 90) * mm, "construction": true});
            skLineSegment(sketch, "E86.MirrorCS", {"start": v(-15, 108) * mm, "end": v(-33, 90) * mm});
            skArc(sketch, "E87.MirrorCS", {"start": v(-15, 120) * mm, "mid": v(0, 135) * mm, "end": v(15, 120) * mm});
            skLineSegment(sketch, "E88.MirrorCS", {"start": v(-15, 120) * mm, "end": v(-15, 108) * mm});
            skLineSegment(sketch, "E89.MirrorCS", {"start": v(15, 108) * mm, "end": v(15, 120) * mm});
            skLineSegment(sketch, "E90.MirrorCS", {"start": v(33, 90) * mm, "end": v(15, 108) * mm});
            skLineSegment(sketch, "E91", {"start": v(-80, 0) * mm, "end": v(80, 0) * mm, "construction": true});
            skLineSegment(sketch, "E92.MirrorCS", {"start": v(-15, -108) * mm, "end": v(-33, -90) * mm});
            skLineSegment(sketch, "E93.MirrorCS", {"start": v(-15, -120) * mm, "end": v(-15, -108) * mm});
            skLineSegment(sketch, "E94.MirrorCS", {"start": v(15, -108) * mm, "end": v(15, -120) * mm});
            skArc(sketch, "E95.MirrorCS", {"start": v(15, -120) * mm, "mid": v(0, -135) * mm, "end": v(-15, -120) * mm});
            skLineSegment(sketch, "E96.MirrorCS", {"start": v(-33, -90) * mm, "end": v(-15, -108) * mm});
            skLineSegment(sketch, "E97.MirrorCS", {"start": v(-15, -108) * mm, "end": v(-15, -120) * mm});
            skCircle(sketch, "E98.MirrorC", {"center": v(0, -120) * mm, "radius": 6 * mm});
            skLineSegment(sketch, "E99.MirrorCS", {"start": v(33, -90) * mm, "end": v(15, -108) * mm});
            skArc(sketch, "E100.MirrorCS", {"start": v(-15, -120) * mm, "mid": v(0, -135) * mm, "end": v(15, -120) * mm});
            skLineSegment(sketch, "E101.MirrorCS", {"start": v(15, -120) * mm, "end": v(15, -108) * mm});
            skLineSegment(sketch, "E102.MirrorCS", {"start": v(15, -108) * mm, "end": v(33, -90) * mm});
            skLineSegment(sketch, "E103.MirrorCS", {"start": v(0, -120) * mm, "end": v(0, -90) * mm, "construction": true});
            skSolve(sketch);
        }
        {
            var Q0;
            Q0=makeQuery(id+"F16.imprint","IMPRINT",FACE,{"disambiguationData":[TD([[makeQuery(id+"F16.imprint","IMPRINT",EDGE,{"derivedFrom":sQuery(id+"F16.wireOp",EDGE,"E84")}),1.0]])]});
            var Q1;
            Q1=makeQuery(id+"F16.imprint","IMPRINT",FACE,{"disambiguationData":[TD([[makeQuery(id+"F16.imprint","IMPRINT",EDGE,{"derivedFrom":sQuery(id+"F16.wireOp",EDGE,"E95.MirrorCS")}),-1.0]])]});
            var Q2;
            Q2=makeQuery(id+"F16.imprint","IMPRINT",FACE,{"disambiguationData":[TD([[makeQuery(id+"F16.imprint","IMPRINT",EDGE,{"derivedFrom":makeQuery(id+"F1.opExtrude","CAP_EDGE",EDGE,{"disambiguationData":[OSD([sQuery(id+"F0.wireOp",EDGE,"E1.left")])],"isStart":true})}),-1.0]])]});
            var Q3;
            Q3=makeQuery(id+"F2.opExtrude","CAP_FACE",FACE,{"disambiguationData":[OSD([sQuery(id+"F0.wireOp",EDGE,"E12"),sQuery(id+"F0.wireOp",EDGE,"E13"),sQuery(id+"F0.wireOp",EDGE,"E14"),sQuery(id+"F0.wireOp",EDGE,"E15"),sQuery(id+"F0.wireOp",EDGE,"E17.filletArc"),sQuery(id+"F0.wireOp",EDGE,"E18.filletArc"),sQuery(id+"F0.wireOp",EDGE,"E19.filletArc"),sQuery(id+"F0.wireOp",EDGE,"E20.filletArc"),sQuery(id+"F0.wireOp",EDGE,"E25.0"),sQuery(id+"F0.wireOp",EDGE,"E25.1"),sQuery(id+"F0.wireOp",EDGE,"E25.2"),sQuery(id+"F0.wireOp",EDGE,"E25.3"),sQuery(id+"F0.wireOp",EDGE,"E25.4"),sQuery(id+"F0.wireOp",EDGE,"E25.5"),sQuery(id+"F0.wireOp",EDGE,"E25.6"),sQuery(id+"F0.wireOp",EDGE,"E25.7")])],"isStart":false});
            extrude(context, id + "F17", {"entities" : qUnion([Q0, Q1, Q2]), "endBound" : BoundingType.UP_TO_SURFACE, "endBoundEntityFace" : qUnion([Q3]), "depth" : 25 * mm});
        }
    });
